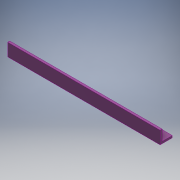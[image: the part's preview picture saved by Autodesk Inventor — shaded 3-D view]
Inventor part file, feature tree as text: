
AUTODESK INVENTOR PART (.ipt)
format: ipt  version: 2018 (Build 220112000, 112)  size: 105,472 bytes
history: native  units: mm
features: extrude x2, sketch x2, projected_geometry x1
ambient origin geometry x8: Origin, YZ Plane, XZ Plane, XY Plane, X Axis, Y Axis, Z Axis, Center Point
bodies: Solid1 (feature_tree)
feature tree (5):
  extrude  "Extrusion1"  Depth=16.0mm
  extrude  "Extrusion2"  Depth=16.0mm
  sketch  "Sketch1"  dims[d0=1200.0mm d1=16.0mm]
  sketch  "Sketch2"  dims[d2=100.0mm d3=0.0mm d4=16.0mm d5=80.0mm d6=0.0mm]
  projected_geometry  "Projected Loop1"
